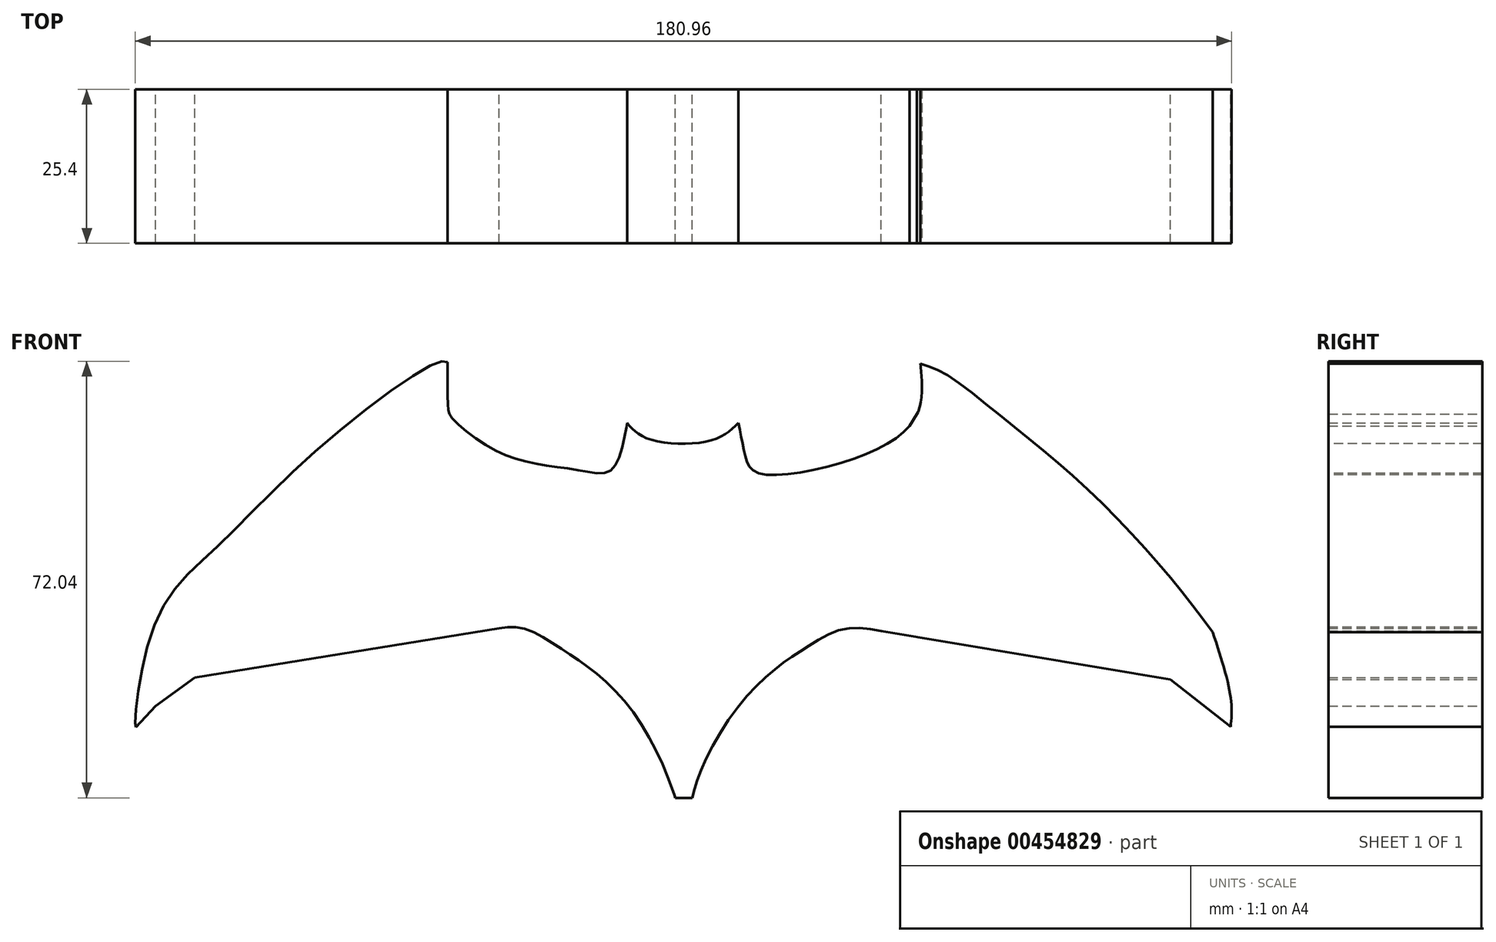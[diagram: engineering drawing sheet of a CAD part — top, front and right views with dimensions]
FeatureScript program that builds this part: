
annotation { "Feature Type Name" : "Feature", "Feature Type Description" : "" }
export const myFeature = defineFeature(function(context is Context, id is Id, definition is map)
    precondition{}
    {
        {
            var Q0;
            Q0=qCreatedBy(makeId("Front.planeOp"),FACE);
            var sketch = newSketch(context, id + "F0", { "sketchPlane" : qUnion([Q0])});
            skFitSpline(sketch, "E0", {"points": [v(-38.95, 37.97) * mm, v(-38.84, 30.26) * mm, v(-38.1, 28.59) * mm, v(-32.25, 24.07) * mm, v(-25.07, 21.35) * mm, v(-17.66, 20.2) * mm, v(-12.65, 19.8) * mm, v(-10.42, 22.92) * mm, v(-9.34, 27.94) * mm, v(-9.34, 27.97) * mm], "startDerivative": vector(-0.75, -63.63) * mm, "endDerivative": vector(-0.3, 1.75) * mm});
            skFitSpline(sketch, "E1", {"points": [v(-38.95, 37.97) * mm, v(-40.5, 37.97) * mm, v(-59.56, 24.36) * mm, v(-77.3, 7.27) * mm, v(-86.11, -2.66) * mm, v(-90.25, -17.98) * mm, v(-90.47, -22.28) * mm, v(-90.44, -22.29) * mm], "startDerivative": vector(-19.53, 6.12) * mm, "endDerivative": vector(3.6, 0.22) * mm});
            skLineSegment(sketch, "E2", {"start": v(-90.44, -22.29) * mm, "end": v(-87.18, -18.78) * mm});
            skLineSegment(sketch, "E3", {"start": v(-87.18, -18.78) * mm, "end": v(-80.72, -14.1) * mm});
            skLineSegment(sketch, "E4", {"start": v(-80.72, -14.1) * mm, "end": v(-30.45, -5.92) * mm});
            skFitSpline(sketch, "E5", {"points": [v(-30.45, -5.92) * mm, v(-26.51, -5.92) * mm, v(-21.2, -8.68) * mm, v(-15.96, -12.22) * mm, v(-9.54, -18.25) * mm, v(-3.37, -28.67) * mm, v(-1.42, -33.82) * mm, v(-1.36, -33.93) * mm], "startDerivative": vector(31.06, 4.18) * mm, "endDerivative": vector(1.95, -3.14) * mm});
            skLineSegment(sketch, "E6", {"start": v(-1.36, -33.93) * mm, "end": v(1.4, -33.93) * mm});
            skFitSpline(sketch, "E7", {"points": [v(1.4, -33.93) * mm, v(3.02, -28.96) * mm, v(9.05, -18.8) * mm, v(15.67, -12.24) * mm, v(20.45, -8.96) * mm, v(26.35, -6.08) * mm, v(32.58, -6.4) * mm], "startDerivative": vector(8.32, 31.96) * mm, "endDerivative": vector(40.9, -7.41) * mm});
            skLineSegment(sketch, "E8", {"start": v(32.58, -6.4) * mm, "end": v(80.32, -14.37) * mm});
            skFitSpline(sketch, "E9", {"points": [v(80.32, -14.37) * mm, v(90.29, -22.2) * mm], "startDerivative": vector(9.97, -7.84) * mm, "endDerivative": vector(9.97, -7.84) * mm});
            skFitSpline(sketch, "E10", {"points": [v(90.29, -22.2) * mm, v(90.29, -17.33) * mm, v(87.32, -6.57) * mm], "startDerivative": vector(0.98, 11.14) * mm, "endDerivative": vector(-6.42, 19.57) * mm});
            skFitSpline(sketch, "E11", {"points": [v(-9.34, 27.94) * mm, v(-5.92, 25.36) * mm, v(4.63, 25.1) * mm, v(9.02, 27.94) * mm], "startDerivative": vector(9.32, -10.74) * mm, "endDerivative": vector(11.47, 11.1) * mm});
            skFitSpline(sketch, "E12", {"points": [v(9.02, 27.94) * mm, v(10.15, 22.62) * mm, v(12.18, 19.73) * mm, v(29.19, 22.45) * mm, v(38.52, 29.4) * mm, v(39.07, 37.74) * mm], "startDerivative": vector(6.9, -35.24) * mm, "endDerivative": vector(-4.21, 44.68) * mm});
            skFitSpline(sketch, "E13", {"points": [v(39.07, 37.74) * mm, v(42.92, 36.18) * mm, v(52.66, 28.86) * mm, v(65.35, 18.22) * mm, v(78.72, 4.33) * mm, v(87.32, -6.57) * mm], "startDerivative": vector(30.54, -9.18) * mm, "endDerivative": vector(37.75, -50.1) * mm});
            skFitSpline(sketch, "E14", {"points": [v(-90.44, -22.29) * mm, v(-84.9, -9.93) * mm, v(-76.1, 0) * mm, v(-47.1, 25.22) * mm, v(-38.95, 37.97) * mm], "startDerivative": vector(24.86, 62.9) * mm, "endDerivative": vector(24.32, 52.26) * mm});
            skFitSpline(sketch, "E15", {"points": [v(90.29, -22.2) * mm, v(84.47, -11.05) * mm, v(69.6, 2.78) * mm, v(49.2, 20.58) * mm, v(39.07, 37.74) * mm], "startDerivative": vector(-23.2, 56.29) * mm, "endDerivative": vector(-32.7, 69.54) * mm});
            skFitSpline(sketch, "E16", {"points": [v(0, -29.74) * mm, v(1.79, -24.63) * mm, v(8.75, -13.36) * mm, v(21.53, -2.93) * mm, v(33.6, -3.26) * mm, v(77.42, -11.05) * mm, v(81.55, -12.03) * mm, v(84.05, -14.37) * mm, v(90.29, -22.2) * mm], "startDerivative": vector(16.39, 54.89) * mm, "endDerivative": vector(59.08, -76.42) * mm});
            skFitSpline(sketch, "E17", {"points": [v(0, -29.74) * mm, v(-2.13, -24.37) * mm, v(-9.54, -12.57) * mm, v(-17.34, -5.76) * mm, v(-22.26, -2.94) * mm, v(-28.95, -2.92) * mm, v(-64.5, -8.68) * mm, v(-80.72, -11.05) * mm, v(-84.42, -14.1) * mm, v(-90.44, -22.29) * mm], "startDerivative": vector(-20.4, 59) * mm, "endDerivative": vector(-60.9, -85.5) * mm});
            skLineSegment(sketch, "E18", {"start": v(-74.22, -9.76) * mm, "end": v(-40.28, 16) * mm});
            skLineSegment(sketch, "E19", {"start": v(-40.28, 16) * mm, "end": v(-40.28, 35.2) * mm});
            skLineSegment(sketch, "E20", {"start": v(-71.4, -9.45) * mm, "end": v(-38.95, 15.02) * mm});
            skLineSegment(sketch, "E21", {"start": v(-38.95, 15.02) * mm, "end": v(38.28, 15.02) * mm});
            skLineSegment(sketch, "E22", {"start": v(38.28, 15.02) * mm, "end": v(71.57, -10.08) * mm});
            skLineSegment(sketch, "E23", {"start": v(-38.1, 28.59) * mm, "end": v(-38.1, 16.29) * mm});
            skLineSegment(sketch, "E24", {"start": v(-38.1, 16.29) * mm, "end": v(37.3, 16.29) * mm});
            skLineSegment(sketch, "E25", {"start": v(37.3, 16.29) * mm, "end": v(37.3, 27.48) * mm});
            skLineSegment(sketch, "E26", {"start": v(37.3, 27.48) * mm, "end": v(38.52, 29.4) * mm});
            skLineSegment(sketch, "E27", {"start": v(74.14, -10.52) * mm, "end": v(38.52, 16.34) * mm});
            skLineSegment(sketch, "E28", {"start": v(38.52, 16.34) * mm, "end": v(38.52, 29.4) * mm});
            skSolve(sketch);
        }
        {
            var Q0;
            Q0 = qSketchRegion(id + "F0", true);
            var Q1;
            {var subQ0=sQuery(id+"F0.wireOp",EDGE,"E20");Q1=makeQuery(id+"F0.imprint","IMPRINT",FACE,{"disambiguationData":[TD([[makeQuery(id+"F0.imprint","IMPRINT",EDGE,{"derivedFrom":subQ0}),-1.0]])]});}
            extrude(context, id + "F1", {"entities" : qUnion([Q0, Q1]), "endBound" : BoundingType.SYMMETRIC, "depth" : 25.4 * mm});
        }
    });
